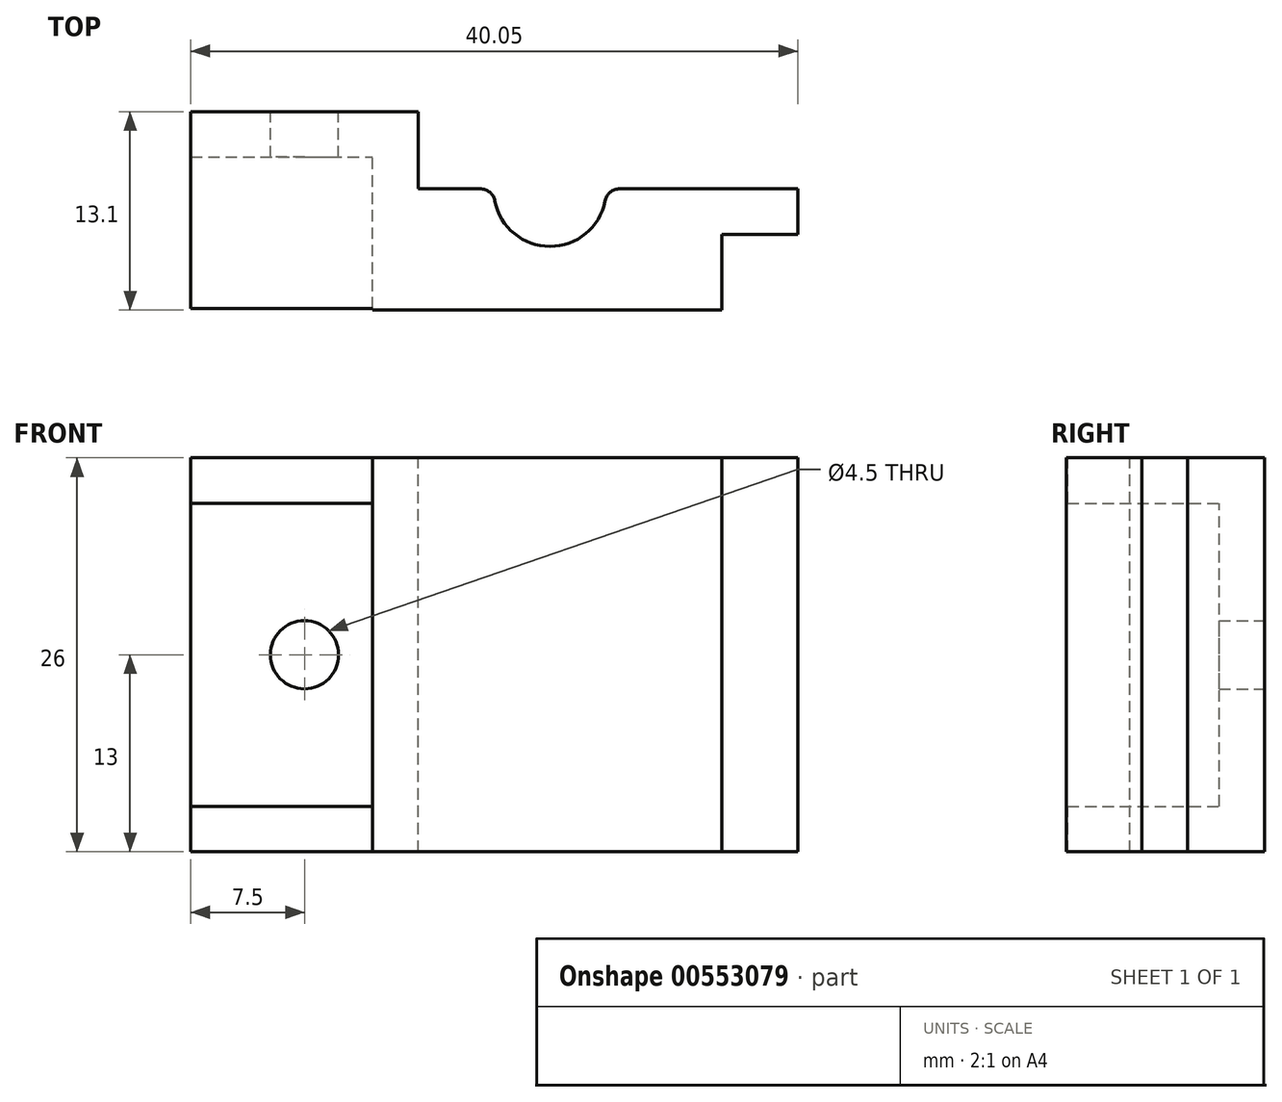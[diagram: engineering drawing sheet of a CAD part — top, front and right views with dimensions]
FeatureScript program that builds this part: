
annotation { "Feature Type Name" : "Feature", "Feature Type Description" : "" }
export const myFeature = defineFeature(function(context is Context, id is Id, definition is map)
    precondition{}
    {
        {
            var Q0;
            Q0=qCreatedBy(makeId("Top.planeOp"),FACE);
            var sketch = newSketch(context, id + "F0", { "sketchPlane" : qUnion([Q0])});
            skLineSegment(sketch, "E0", {"start": v(0, 10.1) * mm, "end": v(12, 10.1) * mm});
            skLineSegment(sketch, "E1", {"start": v(12, 10.1) * mm, "end": v(12, 0) * mm});
            skLineSegment(sketch, "E2", {"start": v(12, 0) * mm, "end": v(35.05, 0) * mm});
            skLineSegment(sketch, "E3", {"start": v(35.05, 0) * mm, "end": v(35.05, 5) * mm});
            skLineSegment(sketch, "E4", {"start": v(35.05, 5) * mm, "end": v(40.05, 5) * mm});
            skLineSegment(sketch, "E5", {"start": v(40.05, 5) * mm, "end": v(40.05, 8) * mm});
            skLineSegment(sketch, "E6", {"start": v(40.05, 8) * mm, "end": v(27.4, 8) * mm});
            skLineSegment(sketch, "E7", {"start": v(27.4, 8) * mm, "end": v(27.4, 7.9) * mm});
            skLineSegment(sketch, "E8", {"start": v(23.7, 4.2) * mm, "end": v(23.7, 4.2) * mm});
            skLineSegment(sketch, "E9", {"start": v(20, 7.9) * mm, "end": v(20, 8) * mm});
            skLineSegment(sketch, "E10", {"start": v(20, 8) * mm, "end": v(15, 8) * mm});
            skLineSegment(sketch, "E11", {"start": v(15, 8) * mm, "end": v(15, 13.1) * mm});
            skLineSegment(sketch, "E12", {"start": v(15, 13.1) * mm, "end": v(0, 13.1) * mm});
            skLineSegment(sketch, "E13", {"start": v(0, 13.1) * mm, "end": v(0, 10.1) * mm});
            skPoint(sketch, "E14.visualSharp", {"position": v(20, 4.2) * mm});
            skArc(sketch, "E14.filletArc", {"start": v(20, 7.9) * mm, "mid": v(21.08, 5.28) * mm, "end": v(23.7, 4.2) * mm});
            skPoint(sketch, "E15.visualSharp", {"position": v(27.4, 4.2) * mm});
            skArc(sketch, "E15.filletArc", {"start": v(23.7, 4.2) * mm, "mid": v(26.32, 5.28) * mm, "end": v(27.4, 7.9) * mm});
            skSolve(sketch);
        }
        {
            var Q0;
            Q0 = qSketchRegion(id + "F0", true);
            extrude(context, id + "F1", {"entities" : qUnion([Q0]), "oppositeDirection" : true, "depth" : 26 * mm, "offsetDistance" : 25 * mm});
        }
        {
            var Q0;
            Q0=makeQuery(id+"F1.opExtrude","SWEPT_FACE",FACE,{"disambiguationData":[OSD([sQuery(id+"F0.wireOp",EDGE,"E0")])]});
            var sketch = newSketch(context, id + "F2", { "sketchPlane" : qUnion([Q0])});
            skLineSegment(sketch, "E16.bottom", {"start": v(0, 0) * mm, "end": v(12, 0) * mm});
            skLineSegment(sketch, "E16.top", {"start": v(0, -3) * mm, "end": v(12, -3) * mm});
            skLineSegment(sketch, "E16.left", {"start": v(0, 0) * mm, "end": v(0, -3) * mm});
            skLineSegment(sketch, "E16.right", {"start": v(12, 0) * mm, "end": v(12, -3) * mm});
            skLineSegment(sketch, "E17.bottom", {"start": v(0, -23) * mm, "end": v(12, -23) * mm});
            skLineSegment(sketch, "E17.top", {"start": v(0, -26) * mm, "end": v(12, -26) * mm});
            skLineSegment(sketch, "E17.left", {"start": v(0, -23) * mm, "end": v(0, -26) * mm});
            skLineSegment(sketch, "E17.right", {"start": v(12, -23) * mm, "end": v(12, -26) * mm});
            skSolve(sketch);
        }
        {
            var Q0;
            Q0 = qSketchRegion(id + "F2", true);
            extrude(context, id + "F3", {"entities" : qUnion([Q0]), "operationType" : NewBodyOperationType.ADD, "depth" : 10 * mm, "offsetDistance" : 25 * mm});
        }
        {
            var Q0;
            Q0=makeQuery(id+"F1.opExtrude","SWEPT_FACE",FACE,{"disambiguationData":[OSD([sQuery(id+"F0.wireOp",EDGE,"E12")])]});
            var sketch = newSketch(context, id + "F4", { "sketchPlane" : qUnion([Q0])});
            skCircle(sketch, "E18", {"center": v(-7.5, -13) * mm, "radius": 2.25 * mm});
            skSolve(sketch);
        }
        {
            var Q0;
            Q0 = qSketchRegion(id + "F4", true);
            extrude(context, id + "F5", {"entities" : qUnion([Q0]), "operationType" : NewBodyOperationType.REMOVE, "endBound" : BoundingType.UP_TO_NEXT, "oppositeDirection" : true, "depth" : 25 * mm, "offsetDistance" : 25 * mm});
        }
        {
            var Q0;
            Q0=makeQuery(id+"F1.opExtrude","SWEPT_EDGE",EDGE,{"disambiguationData":[OSD([sQuery(id+"F0.wireOp",EDGE,"E9"),sQuery(id+"F0.wireOp",EDGE,"E10")])]});
            var Q1;
            Q1=makeQuery(id+"F1.opExtrude","SWEPT_EDGE",EDGE,{"disambiguationData":[OSD([sQuery(id+"F0.wireOp",EDGE,"E6"),sQuery(id+"F0.wireOp",EDGE,"E7")])]});
            fillet(context, id + "F6", {"entities" : qUnion([Q0, Q1]), "radius" : 1 * mm, "tangentPropagation" : true, "allowEdgeOverflow" : false});
        }
    });
